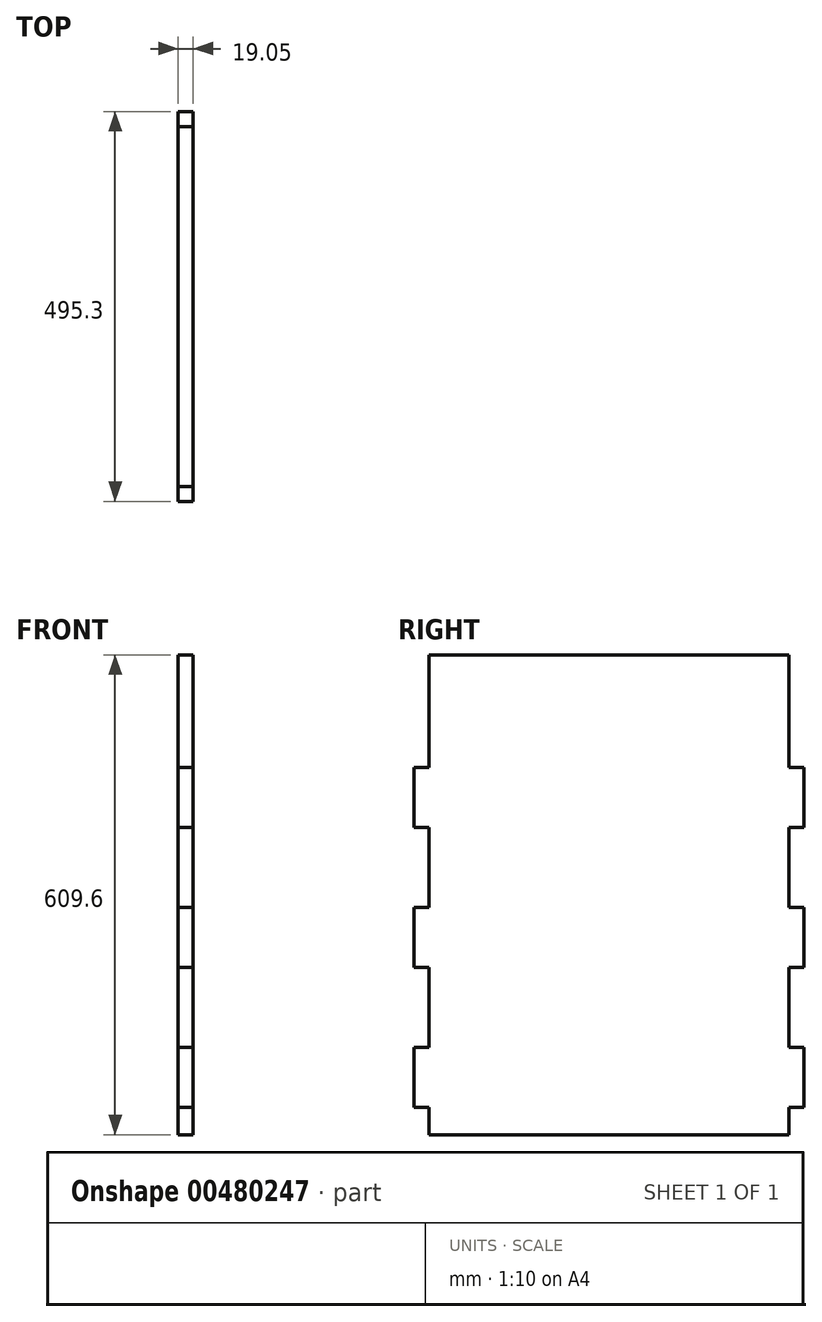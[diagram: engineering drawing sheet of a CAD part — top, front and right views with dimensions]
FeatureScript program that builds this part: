
annotation { "Feature Type Name" : "Feature", "Feature Type Description" : "" }
export const myFeature = defineFeature(function(context is Context, id is Id, definition is map)
    precondition{}
    {
        {
            var Q0;
            Q0=qCreatedBy(makeId("Right.planeOp"),FACE);
            var sketch = newSketch(context, id + "F0", { "sketchPlane" : qUnion([Q0])});
            skLineSegment(sketch, "E0.bottom", {"start": v(0, 0) * mm, "end": v(457.2, 0) * mm});
            skLineSegment(sketch, "E0.top", {"start": v(0, 609.6) * mm, "end": v(457.2, 609.6) * mm});
            skLineSegment(sketch, "E0.left", {"start": v(0, 0) * mm, "end": v(0, 609.6) * mm});
            skLineSegment(sketch, "E0.right", {"start": v(457.2, 0) * mm, "end": v(457.2, 609.6) * mm});
            skLineSegment(sketch, "E1.bottom", {"start": v(457.2, 34.46) * mm, "end": v(476.25, 34.46) * mm});
            skLineSegment(sketch, "E1.top", {"start": v(457.2, 110.66) * mm, "end": v(476.25, 110.66) * mm});
            skLineSegment(sketch, "E1.left", {"start": v(457.2, 34.46) * mm, "end": v(457.2, 110.66) * mm});
            skLineSegment(sketch, "E1.right", {"start": v(476.25, 34.46) * mm, "end": v(476.25, 110.66) * mm});
            skLineSegment(sketch, "E2", {"start": v(457.2, 110.66) * mm, "end": v(457.2, 212.26) * mm, "construction": true});
            skLineSegment(sketch, "E3", {"start": v(457.2, 212.26) * mm, "end": v(457.2, 288.46) * mm});
            skLineSegment(sketch, "E4", {"start": v(457.2, 288.46) * mm, "end": v(457.2, 390.06) * mm, "construction": true});
            skLineSegment(sketch, "E5", {"start": v(457.2, 390.06) * mm, "end": v(457.2, 466.26) * mm});
            skLineSegment(sketch, "E6", {"start": v(457.2, 212.26) * mm, "end": v(476.25, 212.26) * mm});
            skLineSegment(sketch, "E7", {"start": v(457.2, 288.46) * mm, "end": v(476.25, 288.46) * mm});
            skLineSegment(sketch, "E8", {"start": v(457.2, 390.06) * mm, "end": v(476.25, 390.06) * mm});
            skLineSegment(sketch, "E9", {"start": v(457.2, 466.26) * mm, "end": v(476.25, 466.26) * mm});
            skLineSegment(sketch, "E10", {"start": v(476.25, 466.26) * mm, "end": v(476.25, 390.06) * mm});
            skLineSegment(sketch, "E11", {"start": v(476.25, 288.46) * mm, "end": v(476.25, 212.26) * mm});
            skLineSegment(sketch, "E12", {"start": v(228.6, 609.6) * mm, "end": v(228.6, 0) * mm, "construction": true});
            skLineSegment(sketch, "E13.MirrorCS", {"start": v(0, 466.26) * mm, "end": v(-19.05, 466.26) * mm});
            skLineSegment(sketch, "E14.MirrorCS", {"start": v(-19.05, 466.26) * mm, "end": v(-19.05, 390.06) * mm});
            skLineSegment(sketch, "E15.MirrorCS", {"start": v(-19.05, 288.46) * mm, "end": v(-19.05, 212.26) * mm});
            skLineSegment(sketch, "E16.MirrorCS", {"start": v(-19.05, 34.46) * mm, "end": v(-19.05, 110.66) * mm});
            skLineSegment(sketch, "E17.MirrorCS", {"start": v(0, 34.46) * mm, "end": v(-19.05, 34.46) * mm});
            skLineSegment(sketch, "E18.MirrorCS", {"start": v(0, 110.66) * mm, "end": v(-19.05, 110.66) * mm});
            skLineSegment(sketch, "E19.MirrorCS", {"start": v(0, 212.26) * mm, "end": v(-19.05, 212.26) * mm});
            skLineSegment(sketch, "E20.MirrorCS", {"start": v(0, 288.46) * mm, "end": v(-19.05, 288.46) * mm});
            skLineSegment(sketch, "E21.MirrorCS", {"start": v(0, 390.06) * mm, "end": v(-19.05, 390.06) * mm});
            skSolve(sketch);
        }
        {
            var Q0;
            Q0 = qSketchRegion(id + "F0", true);
            extrude(context, id + "F1", {"entities" : qUnion([Q0]), "depth" : 19.05 * mm});
        }
    });
